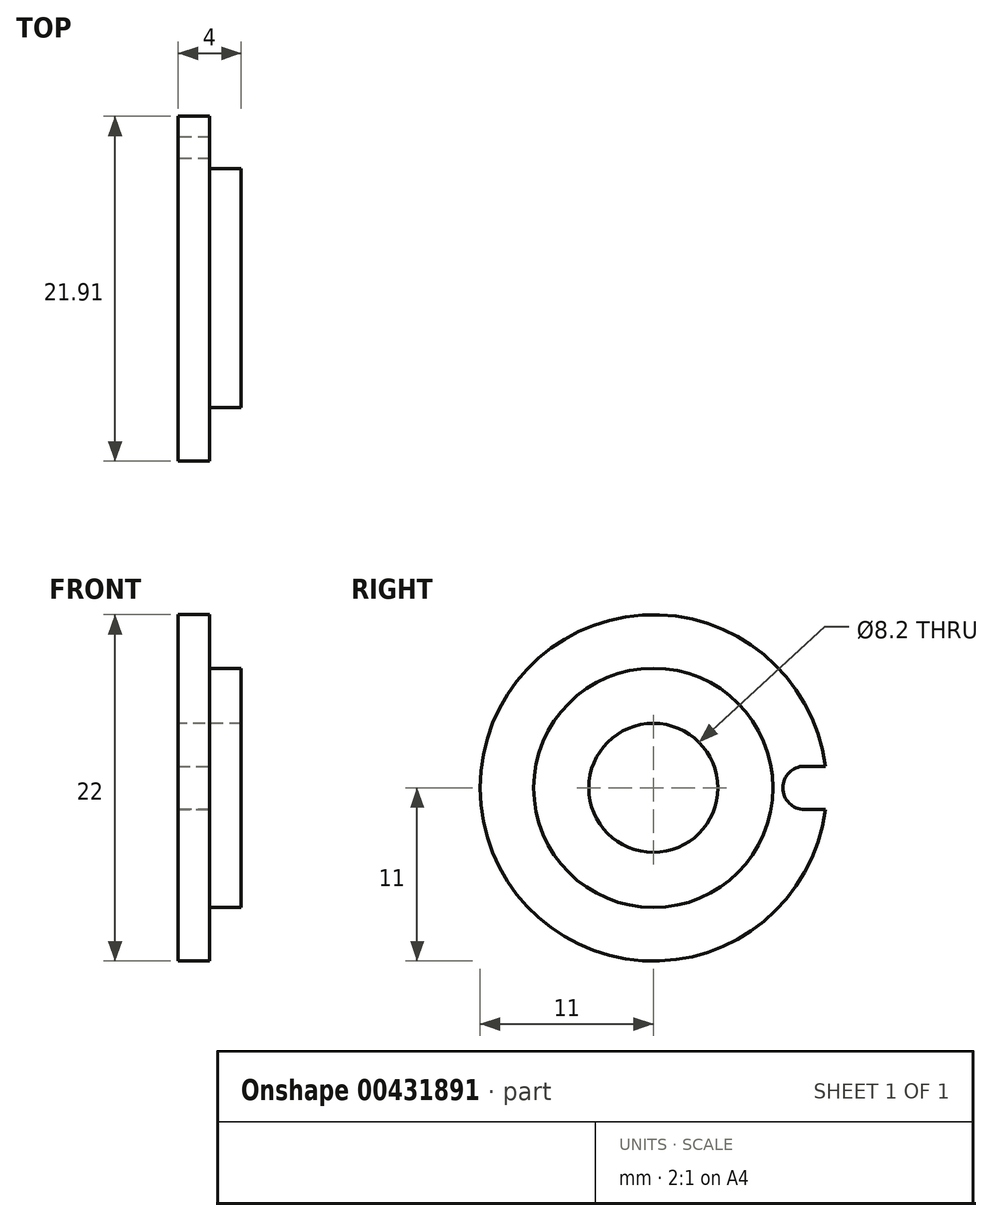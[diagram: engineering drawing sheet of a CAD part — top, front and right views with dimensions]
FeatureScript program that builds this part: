
annotation { "Feature Type Name" : "Feature", "Feature Type Description" : "" }
export const myFeature = defineFeature(function(context is Context, id is Id, definition is map)
    precondition{}
    {
        {
            var Q0;
            Q0=qCreatedBy(makeId("Right.planeOp"),FACE);
            var sketch = newSketch(context, id + "F0", { "sketchPlane" : qUnion([Q0])});
            skCircle(sketch, "E0", {"center": v(0, 0) * mm, "radius": 11 * mm});
            skCircle(sketch, "E1", {"center": v(0, 0) * mm, "radius": 7.6 * mm});
            skSolve(sketch);
        }
        {
            var Q0;
            Q0=makeQuery(id+"F0.imprint","IMPRINT",FACE,{"disambiguationData":[TD([[makeQuery(id+"F0.imprint","IMPRINT",EDGE,{"derivedFrom":sQuery(id+"F0.wireOp",EDGE,"E0")}),1.0]])]});
            var Q1;
            Q1=makeQuery(id+"F0.imprint","IMPRINT",FACE,{"disambiguationData":[TD([[makeQuery(id+"F0.imprint","IMPRINT",EDGE,{"derivedFrom":sQuery(id+"F0.wireOp",EDGE,"E1")}),1.0]])]});
            extrude(context, id + "F1", {"entities" : qUnion([Q0, Q1]), "depth" : -2 * mm});
        }
        {
            var Q0;
            Q0=makeQuery(id+"F0.imprint","IMPRINT",FACE,{"disambiguationData":[TD([[makeQuery(id+"F0.imprint","IMPRINT",EDGE,{"derivedFrom":sQuery(id+"F0.wireOp",EDGE,"E1")}),1.0]])]});
            extrude(context, id + "F2", {"entities" : qUnion([Q0]), "operationType" : NewBodyOperationType.ADD, "depth" : 2 * mm});
        }
        {
            var Q0;
            Q0=makeQuery(id+"F1.opExtrude","CAP_FACE",FACE,{"disambiguationData":[OSD([sQuery(id+"F0.wireOp",EDGE,"E0")])],"isStart":false});
            var sketch = newSketch(context, id + "F3", { "sketchPlane" : qUnion([Q0])});
            skCircle(sketch, "E2", {"center": v(0, 0) * mm, "radius": 4.1 * mm});
            skSolve(sketch);
        }
        {
            var Q0;
            Q0 = qSketchRegion(id + "F3", true);
            extrude(context, id + "F4", {"entities" : qUnion([Q0]), "operationType" : NewBodyOperationType.REMOVE, "oppositeDirection" : true, "depth" : 25 * mm});
        }
        {
            var Q0;
            Q0=makeQuery(id+"F1.opExtrude","CAP_FACE",FACE,{"disambiguationData":[OSD([sQuery(id+"F0.wireOp",EDGE,"E0")])],"isStart":false});
            var sketch = newSketch(context, id + "F5", { "sketchPlane" : qUnion([Q0])});
            skCircle(sketch, "E3", {"center": v(-9.6, 0) * mm, "radius": 1.38 * mm});
            skLineSegment(sketch, "E4.bottom", {"start": v(-9.6, 1.38) * mm, "end": v(-11.63, 1.37) * mm});
            skLineSegment(sketch, "E4.top", {"start": v(-9.6, -1.38) * mm, "end": v(-11.63, -1.38) * mm});
            skLineSegment(sketch, "E4.left", {"start": v(-9.6, 1.38) * mm, "end": v(-9.6, -1.38) * mm});
            skLineSegment(sketch, "E4.right", {"start": v(-11.63, 1.37) * mm, "end": v(-11.63, -1.38) * mm});
            skSolve(sketch);
        }
        {
            var Q0;
            {var subQ0=sQuery(id+"F5.wireOp",EDGE,"E4.right");Q0=makeQuery(id+"F5.imprint","IMPRINT",FACE,{"disambiguationData":[TD([[makeQuery(id+"F5.imprint","IMPRINT",EDGE,{"derivedFrom":subQ0}),1.0]])]});}
            var Q1;
            {var subQ0=sQuery(id+"F5.wireOp",EDGE,"E4.bottom");var subQ3=makeQuery(id+"F1.opExtrude","CAP_EDGE",EDGE,{"disambiguationData":[OSD([sQuery(id+"F0.wireOp",EDGE,"E0")])],"isStart":false});var subQ5=makeQuery(id+"F5.imprint","INTERSECT",VERTEX,{"derivedFrom":[subQ3,subQ0]});Q1=makeQuery(id+"F5.imprint","IMPRINT",FACE,{"disambiguationData":[TD([[makeQuery(id+"F5.imprint","IMPRINT",EDGE,{"disambiguationData":[TD([[subQ5,1.0]])],"derivedFrom":subQ3}),-1.0]])]});}
            var Q2;
            {var subQ0=sQuery(id+"F5.wireOp",EDGE,"E3");var subQ1=makeQuery(id+"F1.opExtrude","CAP_EDGE",EDGE,{"disambiguationData":[OSD([sQuery(id+"F0.wireOp",EDGE,"E0")])],"isStart":false});var subQ2=makeQuery(id+"F5.imprint","INTERSECT",VERTEX,{"disambiguationData":[OD(0.0)],"derivedFrom":[subQ1,subQ0]});Q2=makeQuery(id+"F5.imprint","IMPRINT",FACE,{"disambiguationData":[TD([[makeQuery(id+"F5.imprint","IMPRINT",EDGE,{"disambiguationData":[TD([[subQ2,-1.0]])],"derivedFrom":subQ0}),1.0]])]});}
            var Q3;
            {var subQ0=sQuery(id+"F5.wireOp",EDGE,"E4.left");var subQ1=sQuery(id+"F5.wireOp",EDGE,"E3");var subQ6=makeQuery(id+"F5.imprint","INTERSECT",VERTEX,{"derivedFrom":[subQ1,subQ0]});Q3=makeQuery(id+"F5.imprint","IMPRINT",FACE,{"disambiguationData":[TD([[makeQuery(id+"F5.imprint","IMPRINT",EDGE,{"disambiguationData":[TD([[subQ6,1.0]])],"derivedFrom":subQ1}),1.0]])]});}
            var Q4;
            {var subQ0=sQuery(id+"F5.wireOp",EDGE,"E4.left");var subQ1=sQuery(id+"F5.wireOp",EDGE,"E3");var subQ2=makeQuery(id+"F5.imprint","INTERSECT",VERTEX,{"derivedFrom":[subQ1,subQ0]});Q4=makeQuery(id+"F5.imprint","IMPRINT",FACE,{"disambiguationData":[TD([[makeQuery(id+"F5.imprint","IMPRINT",EDGE,{"disambiguationData":[TD([[subQ2,1.0]])],"derivedFrom":subQ1}),-1.0]])]});}
            var Q5;
            {var subQ0=sQuery(id+"F5.wireOp",EDGE,"E4.left");var subQ1=sQuery(id+"F5.wireOp",EDGE,"E3");var subQ3=makeQuery(id+"F5.imprint","INTERSECT",VERTEX,{"derivedFrom":[subQ1,subQ0]});Q5=makeQuery(id+"F5.imprint","IMPRINT",FACE,{"disambiguationData":[TD([[makeQuery(id+"F5.imprint","IMPRINT",EDGE,{"disambiguationData":[TD([[subQ3,-1.0]])],"derivedFrom":subQ1}),1.0]])]});}
            extrude(context, id + "F6", {"entities" : qUnion([Q0, Q1, Q2, Q3, Q4, Q5]), "operationType" : NewBodyOperationType.REMOVE, "oppositeDirection" : true, "depth" : 5 * mm});
        }
    });
